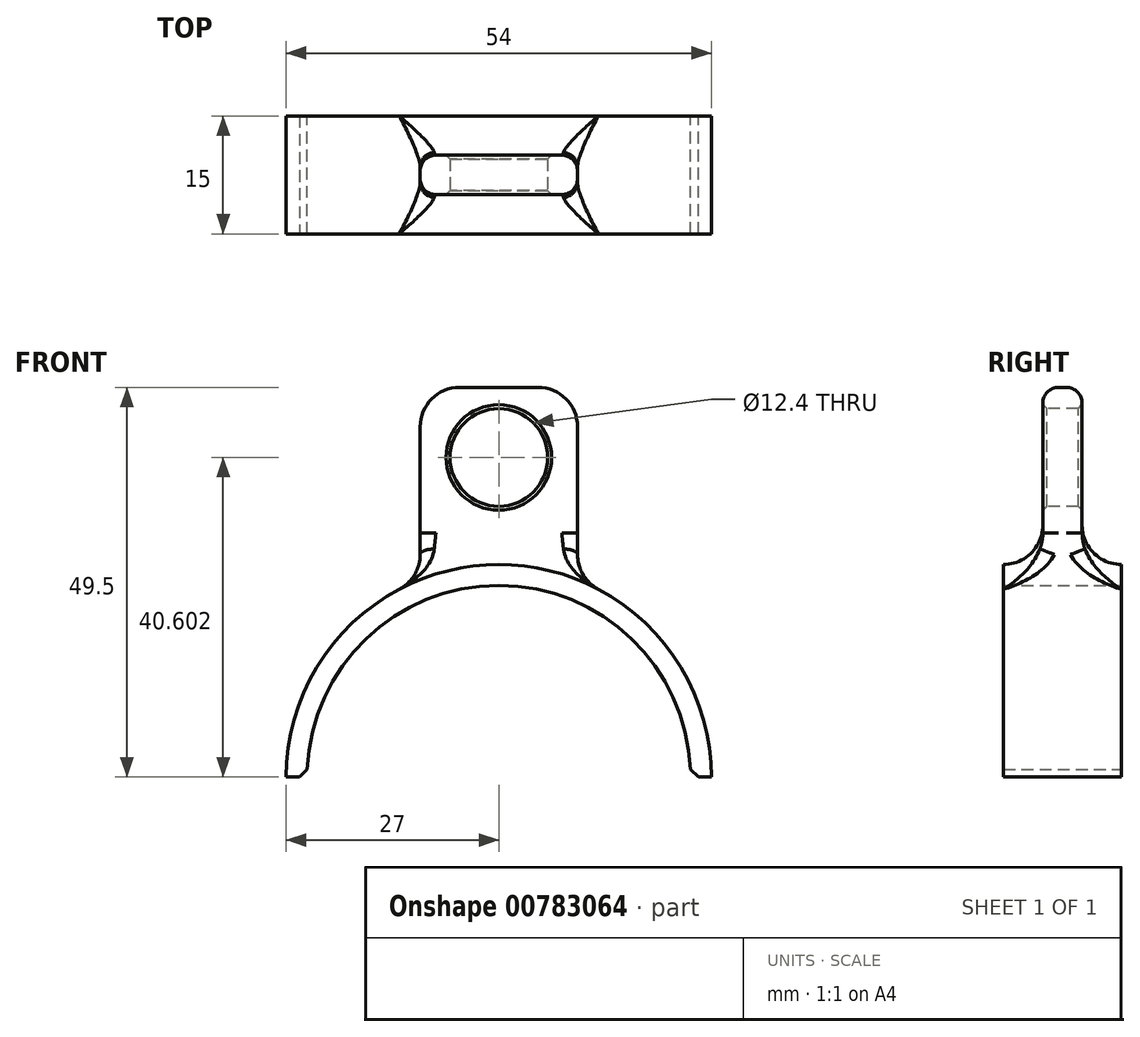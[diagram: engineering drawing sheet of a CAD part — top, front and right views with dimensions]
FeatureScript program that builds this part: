
annotation { "Feature Type Name" : "Feature", "Feature Type Description" : "" }
export const myFeature = defineFeature(function(context is Context, id is Id, definition is map)
    precondition{}
    {
        {
            var Q0;
            Q0=qCreatedBy(makeId("Front.planeOp"),FACE);
            var sketch = newSketch(context, id + "F0", { "sketchPlane" : qUnion([Q0])});
            skArc(sketch, "E0.0", {"start": v(27, 0) * mm, "mid": v(0, 27) * mm, "end": v(-27, 0) * mm});
            skLineSegment(sketch, "E1", {"start": v(-27, 0) * mm, "end": v(27, 0) * mm});
            skSolve(sketch);
        }
        {
            var Q0;
            Q0=makeQuery(id+"F0.imprint","IMPRINT",FACE,{"disambiguationData":[TD([[makeQuery(id+"F0.imprint","IMPRINT",EDGE,{"derivedFrom":sQuery(id+"F0.wireOp",EDGE,"E0.0")}),1.0]])]});
            extrude(context, id + "F1", {"entities" : qUnion([Q0]), "depth" : 15 * mm, "offsetDistance" : 25 * mm});
        }
        {
            var Q0;
            Q0=qCreatedBy(makeId("Front.planeOp"),FACE);
            var sketch = newSketch(context, id + "F2", { "sketchPlane" : qUnion([Q0])});
            skCircle(sketch, "E2", {"center": v(0, 0) * mm, "radius": 24.35 * mm});
            skSolve(sketch);
        }
        {
            var Q0;
            Q0=makeQuery(id+"F2.imprint","IMPRINT",FACE,{"disambiguationData":[TD([[makeQuery(id+"F2.imprint","IMPRINT",EDGE,{"derivedFrom":sQuery(id+"F2.wireOp",EDGE,"E2")}),1.0]])]});
            extrude(context, id + "F3", {"entities" : qUnion([Q0]), "operationType" : NewBodyOperationType.REMOVE, "endBound" : BoundingType.SYMMETRIC, "depth" : 45 * mm, "offsetDistance" : 25 * mm});
        }
        {
            var Q0;
            Q0=makeQuery(id+"F1.opExtrude","SWEPT_BODY",BODY,{"disambiguationData":[OSD([sQuery(id+"F0.wireOp",EDGE,"E0.0"),sQuery(id+"F0.wireOp",EDGE,"E1")])]});
            var Q1;
            Q1=qCreatedBy(makeId("Origin.pointOp"),VERTEX);
            var Q2;
            {var subQ0=sQuery(id+"F0.wireOp",EDGE,"E1");Q2=makeQuery(id+"F3.boolean.opBoolean","INTERSECT",VERTEX,{"disambiguationData":[OD(0.0)],"derivedFrom":[makeQuery(id+"F1.opExtrude","CAP_FACE",FACE,{"disambiguationData":[OSD([sQuery(id+"F0.wireOp",EDGE,"E0.0"),subQ0])],"isStart":true}),makeQuery(id+"F1.opExtrude","SWEPT_FACE",FACE,{"disambiguationData":[OSD([subQ0])]}),makeQuery(id+"F3.opExtrude","SWEPT_FACE",FACE,{"disambiguationData":[OSD([sQuery(id+"F2.wireOp",EDGE,"E2")])]})]});}
            transform(context, id + "F4", {"entities" : qUnion([Q0]), "transformType" : TransformType.TRANSLATION_3D, "dx" : 0 * mm, "dy" : 7.5 * mm, "dz" : 0 * mm, "makeCopy" : false});
        }
        {
            var Q0;
            Q0=qCreatedBy(makeId("Front.planeOp"),FACE);
            var sketch = newSketch(context, id + "F5", { "sketchPlane" : qUnion([Q0])});
            skLineSegment(sketch, "E3.bottom", {"start": v(-10, 24.5) * mm, "end": v(10, 24.5) * mm});
            skLineSegment(sketch, "E3.top", {"start": v(-10, 49.5) * mm, "end": v(10, 49.5) * mm});
            skLineSegment(sketch, "E3.left", {"start": v(-10, 24.5) * mm, "end": v(-10, 49.5) * mm});
            skLineSegment(sketch, "E3.right", {"start": v(10, 24.5) * mm, "end": v(10, 49.5) * mm});
            skSolve(sketch);
        }
        {
            var Q0;
            Q0=makeQuery(id+"F5.imprint","IMPRINT",FACE,{"disambiguationData":[TD([[makeQuery(id+"F5.imprint","IMPRINT",EDGE,{"derivedFrom":sQuery(id+"F5.wireOp",EDGE,"E3.bottom")}),1.0]])]});
            extrude(context, id + "F6", {"entities" : qUnion([Q0]), "operationType" : NewBodyOperationType.ADD, "endBound" : BoundingType.SYMMETRIC, "depth" : 5 * mm, "offsetDistance" : 25 * mm});
        }
        {
            var Q0;
            Q0=makeQuery(id+"F6.opExtrude","CAP_FACE",FACE,{"disambiguationData":[OSD([sQuery(id+"F5.wireOp",EDGE,"E3.bottom"),sQuery(id+"F5.wireOp",EDGE,"E3.top"),sQuery(id+"F5.wireOp",EDGE,"E3.left"),sQuery(id+"F5.wireOp",EDGE,"E3.right")])],"isStart":false});
            var sketch = newSketch(context, id + "F7", { "sketchPlane" : qUnion([Q0])});
            skLineSegment(sketch, "E4", {"start": v(-10, 49.5) * mm, "end": v(0, 49.5) * mm, "construction": true});
            skLineSegment(sketch, "E5", {"start": v(0, 49.5) * mm, "end": v(0, 27) * mm, "construction": true});
            skCircle(sketch, "E6", {"center": v(0, 40.6) * mm, "radius": 6.2 * mm});
            skSolve(sketch);
        }
        {
            var Q0;
            Q0=makeQuery(id+"F7.imprint","IMPRINT",FACE,{"disambiguationData":[TD([[makeQuery(id+"F7.imprint","IMPRINT",EDGE,{"derivedFrom":sQuery(id+"F7.wireOp",EDGE,"E6")}),1.0]])]});
            extrude(context, id + "F8", {"entities" : qUnion([Q0]), "operationType" : NewBodyOperationType.REMOVE, "endBound" : BoundingType.SYMMETRIC, "oppositeDirection" : true, "depth" : 25 * mm, "offsetDistance" : 25 * mm});
        }
        {
            var Q0;
            Q0=makeQuery(id+"F6.opExtrude","SWEPT_EDGE",EDGE,{"disambiguationData":[OSD([sQuery(id+"F5.wireOp",EDGE,"E3.top"),sQuery(id+"F5.wireOp",EDGE,"E3.right")])]});
            var Q1;
            Q1=makeQuery(id+"F6.opExtrude","SWEPT_EDGE",EDGE,{"disambiguationData":[OSD([sQuery(id+"F5.wireOp",EDGE,"E3.top"),sQuery(id+"F5.wireOp",EDGE,"E3.left")])]});
            fillet(context, id + "F9", {"entities" : qUnion([Q0, Q1]), "radius" : 5 * mm, "tangentPropagation" : true, "allowEdgeOverflow" : false});
        }
        {
            var Q0;
            Q0=makeQuery(id+"F6.boolean.opBoolean","INTERSECT",EDGE,{"derivedFrom":[makeQuery(id+"F1.opExtrude","SWEPT_FACE",FACE,{"disambiguationData":[OSD([sQuery(id+"F0.wireOp",EDGE,"E0.0")])]}),makeQuery(id+"F6.opExtrude","CAP_FACE",FACE,{"disambiguationData":[OSD([sQuery(id+"F5.wireOp",EDGE,"E3.bottom"),sQuery(id+"F5.wireOp",EDGE,"E3.top"),sQuery(id+"F5.wireOp",EDGE,"E3.left"),sQuery(id+"F5.wireOp",EDGE,"E3.right")])],"isStart":false})]});
            var Q1;
            Q1=makeQuery(id+"F6.boolean.opBoolean","INTERSECT",EDGE,{"derivedFrom":[makeQuery(id+"F1.opExtrude","SWEPT_FACE",FACE,{"disambiguationData":[OSD([sQuery(id+"F0.wireOp",EDGE,"E0.0")])]}),makeQuery(id+"F6.opExtrude","SWEPT_FACE",FACE,{"disambiguationData":[OSD([sQuery(id+"F5.wireOp",EDGE,"E3.right")])]})]});
            var Q2;
            Q2=makeQuery(id+"F6.boolean.opBoolean","INTERSECT",EDGE,{"derivedFrom":[makeQuery(id+"F1.opExtrude","SWEPT_FACE",FACE,{"disambiguationData":[OSD([sQuery(id+"F0.wireOp",EDGE,"E0.0")])]}),makeQuery(id+"F6.opExtrude","CAP_FACE",FACE,{"disambiguationData":[OSD([sQuery(id+"F5.wireOp",EDGE,"E3.bottom"),sQuery(id+"F5.wireOp",EDGE,"E3.top"),sQuery(id+"F5.wireOp",EDGE,"E3.left"),sQuery(id+"F5.wireOp",EDGE,"E3.right")])],"isStart":true})]});
            var Q3;
            Q3=makeQuery(id+"F6.boolean.opBoolean","INTERSECT",EDGE,{"derivedFrom":[makeQuery(id+"F1.opExtrude","SWEPT_FACE",FACE,{"disambiguationData":[OSD([sQuery(id+"F0.wireOp",EDGE,"E0.0")])]}),makeQuery(id+"F6.opExtrude","SWEPT_FACE",FACE,{"disambiguationData":[OSD([sQuery(id+"F5.wireOp",EDGE,"E3.left")])]})]});
            fillet(context, id + "F10", {"entities" : qUnion([Q0, Q1, Q2, Q3]), "radius" : 5 * mm, "tangentPropagation" : true, "allowEdgeOverflow" : false});
        }
        {
            var Q0;
            {var subQ0=sQuery(id+"F5.wireOp",EDGE,"E3.left");var subQ1=makeQuery(id+"F1.opExtrude","SWEPT_FACE",FACE,{"disambiguationData":[OSD([sQuery(id+"F0.wireOp",EDGE,"E0.0")])]});Q0=makeQuery(id+"F10.opFillet","BLEND_EDGE",EDGE,{"blendedFrom":[makeQuery(id+"F6.boolean.opBoolean","INTERSECT",EDGE,{"derivedFrom":[subQ1,makeQuery(id+"F6.opExtrude","CAP_FACE",FACE,{"disambiguationData":[OSD([sQuery(id+"F5.wireOp",EDGE,"E3.bottom"),sQuery(id+"F5.wireOp",EDGE,"E3.top"),subQ0,sQuery(id+"F5.wireOp",EDGE,"E3.right")])],"isStart":false})]}),makeQuery(id+"F6.boolean.opBoolean","INTERSECT",EDGE,{"derivedFrom":[subQ1,makeQuery(id+"F6.opExtrude","SWEPT_FACE",FACE,{"disambiguationData":[OSD([subQ0])]})]})],"blendedInto":[]});}
            var Q1;
            {var subQ0=sQuery(id+"F5.wireOp",EDGE,"E3.right");var subQ1=makeQuery(id+"F1.opExtrude","SWEPT_FACE",FACE,{"disambiguationData":[OSD([sQuery(id+"F0.wireOp",EDGE,"E0.0")])]});Q1=makeQuery(id+"F10.opFillet","BLEND_EDGE",EDGE,{"blendedFrom":[makeQuery(id+"F6.boolean.opBoolean","INTERSECT",EDGE,{"derivedFrom":[subQ1,makeQuery(id+"F6.opExtrude","CAP_FACE",FACE,{"disambiguationData":[OSD([sQuery(id+"F5.wireOp",EDGE,"E3.bottom"),sQuery(id+"F5.wireOp",EDGE,"E3.top"),sQuery(id+"F5.wireOp",EDGE,"E3.left"),subQ0])],"isStart":true})]}),makeQuery(id+"F6.boolean.opBoolean","INTERSECT",EDGE,{"derivedFrom":[subQ1,makeQuery(id+"F6.opExtrude","SWEPT_FACE",FACE,{"disambiguationData":[OSD([subQ0])]})]})],"blendedInto":[]});}
            var Q2;
            {var subQ0=sQuery(id+"F5.wireOp",EDGE,"E3.right");var subQ1=makeQuery(id+"F1.opExtrude","SWEPT_FACE",FACE,{"disambiguationData":[OSD([sQuery(id+"F0.wireOp",EDGE,"E0.0")])]});Q2=makeQuery(id+"F10.opFillet","BLEND_EDGE",EDGE,{"blendedFrom":[makeQuery(id+"F6.boolean.opBoolean","INTERSECT",EDGE,{"derivedFrom":[subQ1,makeQuery(id+"F6.opExtrude","CAP_FACE",FACE,{"disambiguationData":[OSD([sQuery(id+"F5.wireOp",EDGE,"E3.bottom"),sQuery(id+"F5.wireOp",EDGE,"E3.top"),sQuery(id+"F5.wireOp",EDGE,"E3.left"),subQ0])],"isStart":false})]}),makeQuery(id+"F6.boolean.opBoolean","INTERSECT",EDGE,{"derivedFrom":[subQ1,makeQuery(id+"F6.opExtrude","SWEPT_FACE",FACE,{"disambiguationData":[OSD([subQ0])]})]})],"blendedInto":[]});}
            var Q3;
            {var subQ0=sQuery(id+"F5.wireOp",EDGE,"E3.left");var subQ1=makeQuery(id+"F1.opExtrude","SWEPT_FACE",FACE,{"disambiguationData":[OSD([sQuery(id+"F0.wireOp",EDGE,"E0.0")])]});Q3=makeQuery(id+"F10.opFillet","BLEND_EDGE",EDGE,{"blendedFrom":[makeQuery(id+"F6.boolean.opBoolean","INTERSECT",EDGE,{"derivedFrom":[subQ1,makeQuery(id+"F6.opExtrude","CAP_FACE",FACE,{"disambiguationData":[OSD([sQuery(id+"F5.wireOp",EDGE,"E3.bottom"),sQuery(id+"F5.wireOp",EDGE,"E3.top"),subQ0,sQuery(id+"F5.wireOp",EDGE,"E3.right")])],"isStart":true})]}),makeQuery(id+"F6.boolean.opBoolean","INTERSECT",EDGE,{"derivedFrom":[subQ1,makeQuery(id+"F6.opExtrude","SWEPT_FACE",FACE,{"disambiguationData":[OSD([subQ0])]})]})],"blendedInto":[]});}
            fillet(context, id + "F11", {"entities" : qUnion([Q0, Q1, Q2, Q3]), "radius" : 2 * mm, "tangentPropagation" : true, "allowEdgeOverflow" : false});
        }
        {
            var Q0;
            Q0=makeQuery(id+"F8.boolean.opBoolean","INTERSECT",EDGE,{"derivedFrom":[makeQuery(id+"F6.opExtrude","CAP_FACE",FACE,{"disambiguationData":[OSD([sQuery(id+"F5.wireOp",EDGE,"E3.bottom"),sQuery(id+"F5.wireOp",EDGE,"E3.top"),sQuery(id+"F5.wireOp",EDGE,"E3.left"),sQuery(id+"F5.wireOp",EDGE,"E3.right")])],"isStart":true}),makeQuery(id+"F8.opExtrude","SWEPT_FACE",FACE,{"disambiguationData":[OSD([sQuery(id+"F7.wireOp",EDGE,"E6")])]})]});
            var Q1;
            Q1=makeQuery(id+"F8.boolean.opBoolean","INTERSECT",EDGE,{"derivedFrom":[makeQuery(id+"F6.opExtrude","CAP_FACE",FACE,{"disambiguationData":[OSD([sQuery(id+"F5.wireOp",EDGE,"E3.bottom"),sQuery(id+"F5.wireOp",EDGE,"E3.top"),sQuery(id+"F5.wireOp",EDGE,"E3.left"),sQuery(id+"F5.wireOp",EDGE,"E3.right")])],"isStart":false}),makeQuery(id+"F8.opExtrude","SWEPT_FACE",FACE,{"disambiguationData":[OSD([sQuery(id+"F7.wireOp",EDGE,"E6")])]})]});
            chamfer(context, id + "F12", {"entities" : qUnion([Q0, Q1]), "width" : 0.5 * mm, "tangentPropagation" : true});
        }
        {
            var Q0;
            Q0=makeQuery(id+"F3.boolean.opBoolean","INTERSECT",EDGE,{"disambiguationData":[OD(0.0)],"derivedFrom":[makeQuery(id+"F1.opExtrude","SWEPT_FACE",FACE,{"disambiguationData":[OSD([sQuery(id+"F0.wireOp",EDGE,"E1")])]}),makeQuery(id+"F3.opExtrude","SWEPT_FACE",FACE,{"disambiguationData":[OSD([sQuery(id+"F2.wireOp",EDGE,"E2")])]})]});
            var Q1;
            Q1=makeQuery(id+"F3.boolean.opBoolean","INTERSECT",EDGE,{"disambiguationData":[OD(1.0)],"derivedFrom":[makeQuery(id+"F1.opExtrude","SWEPT_FACE",FACE,{"disambiguationData":[OSD([sQuery(id+"F0.wireOp",EDGE,"E1")])]}),makeQuery(id+"F3.opExtrude","SWEPT_FACE",FACE,{"disambiguationData":[OSD([sQuery(id+"F2.wireOp",EDGE,"E2")])]})]});
            chamfer(context, id + "F13", {"entities" : qUnion([Q0, Q1]), "width" : 1 * mm, "tangentPropagation" : true});
        }
    });
